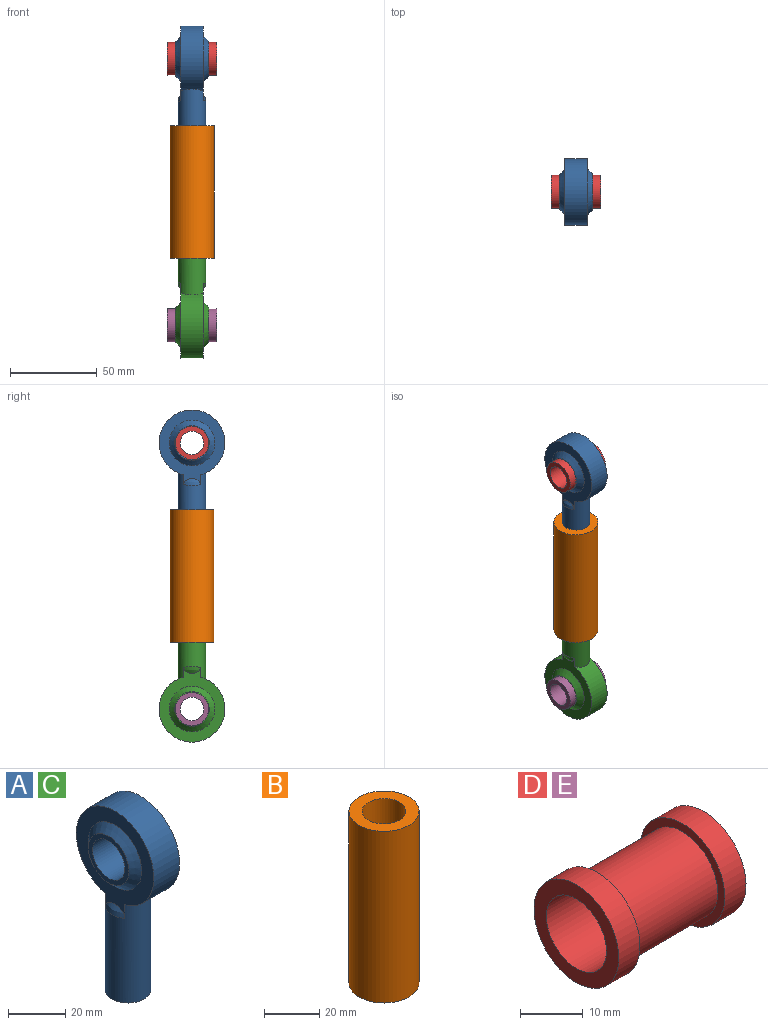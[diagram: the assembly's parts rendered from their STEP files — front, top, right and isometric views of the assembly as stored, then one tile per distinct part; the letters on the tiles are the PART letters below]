
ASSEMBLY  parts=5 mates=4
PART A: 12 faces, bbox 27.1x46.1x87.4 mm
  f0: cylinder r=19.05mm len=38.1mm, axis (-1,0,0), area 1338.3mm2, adj f1,f6,f7
  f1: cylinder r=7.94mm len=41.88mm, axis (0,0,1), area 1971.4mm2, adj f0,f5,f6,f7,f10,f11
  f2: plane 19.88x19.88mm, normal (-1,0,0), area 112.3mm2, adj f4,f8
  f3: plane 20.64x20.64mm, normal (1,0,0), area 136.6mm2, adj f4,f9
  f4: cylinder r=7.94mm len=19.05mm, axis (-1,0,0), area 950.1mm2, adj f2,f3
  f5: plane 15.88x15.88mm, normal (0,0,-1), area 197.9mm2, adj f1
  f6: plane 43.15x38.1mm, normal (1,0,0), area 590.5mm2, adj f0,f1,f9,f11
  f7: plane 51.32x46.13mm, normal (-1,0,0), area 623.7mm2, adj f0,f1,f8,f10
  f8: cone r=9.94mm half-angle=45deg, axis (1,0,0), area 325.2mm2, adj f2,f7
  f9: cone r=10.32mm half-angle=45deg, axis (-1,0,0), area 335.9mm2, adj f3,f6
  f10: bspline ~10.92x5.97mm, area 0mm2, adj f1,f7
  f11: bspline ~10.92x5.97mm, area 31.9mm2, adj f1,f6
PART B: 4 faces, bbox 25.4x25.4x76.2 mm
  f0: cylinder r=7.94mm len=76.2mm, axis (0,0,-1), area 3800.3mm2, adj f2,f3
  f1: cylinder r=12.7mm len=76.2mm, axis (0,0,-1), area 6080.5mm2, adj f2,f3
  f2: plane 25.4x25.4mm, normal (0,0,1), area 308.8mm2, adj f0,f1
  f3: plane 25.4x25.4mm, normal (0,0,-1), area 308.8mm2, adj f0,f1
PART C: same geometry as A
PART D: 8 faces, bbox 28.5x19.1x19.1 mm
  f0: cylinder r=7.94mm len=19.05mm, axis (-1,0,0), area 950.1mm2, adj f5,f7
  f1: cylinder r=6.74mm len=28.55mm, axis (-1,0,0), area 1209.7mm2, adj f2,f3
  f2: plane 19.05x19.05mm, normal (1,0,0), area 142.2mm2, adj f1,f4
  f3: plane 19.05x19.05mm, normal (-1,0,0), area 142.2mm2, adj f1,f6
  f4: cylinder r=9.53mm len=19.05mm, axis (1,0,0), area 284.3mm2, adj f2,f5
  f5: plane 19.05x19.05mm, normal (-1,0,0), area 87.1mm2, adj f0,f4
  f6: cylinder r=9.53mm len=19.05mm, axis (-1,0,0), area 284.3mm2, adj f3,f7
  f7: plane 19.05x19.05mm, normal (1,0,0), area 87.1mm2, adj f0,f6
PART E: same geometry as D
PLACE A t=(-19.22,-9,79.92)mm
PLACE B t=(-19.22,-9,3.14)mm fixed
PLACE C rot(axis=(1,0,0),180deg) t=(-19.22,-9,-73.64)mm
PLACE D t=(-19.22,-9,79.92)mm
PLACE E t=(-19.22,-9,-73.64)mm
MATE fastened D.f0 <-> A.f4  axis (-1,0,0) through (-9.7,-9,79.92)mm
MATE slider A.f1 <-> B.f0  axis (0,0,1) through (-19.22,-9,41.24)mm
MATE slider C.f1 <-> B.f1  axis (0,0,-1) through (-19.22,-9,-34.96)mm
MATE fastened E.f0 <-> C.f4  axis (-1,0,0) through (-9.7,-9,-73.64)mm
